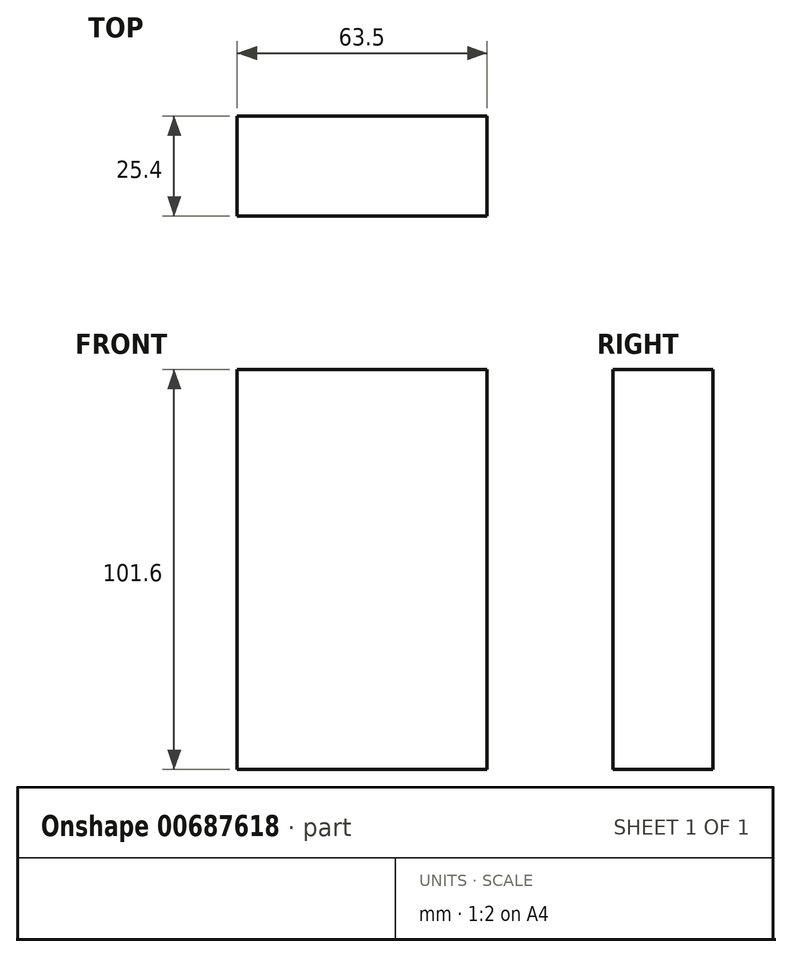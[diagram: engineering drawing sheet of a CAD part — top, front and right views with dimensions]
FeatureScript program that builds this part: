
annotation { "Feature Type Name" : "Feature", "Feature Type Description" : "" }
export const myFeature = defineFeature(function(context is Context, id is Id, definition is map)
    precondition{}
    {
        {
            var Q0;
            Q0=qCreatedBy(makeId("Front.planeOp"),FACE);
            var sketch = newSketch(context, id + "F0", { "sketchPlane" : qUnion([Q0])});
            skLineSegment(sketch, "E0.bottom", {"start": v(-39.98, 42.68) * mm, "end": v(23.52, 42.68) * mm});
            skLineSegment(sketch, "E0.top", {"start": v(-39.98, -58.92) * mm, "end": v(23.52, -58.92) * mm});
            skLineSegment(sketch, "E0.left", {"start": v(-39.98, 42.68) * mm, "end": v(-39.98, -58.92) * mm});
            skLineSegment(sketch, "E0.right", {"start": v(23.52, 42.68) * mm, "end": v(23.52, -58.92) * mm});
            skSolve(sketch);
        }
        {
            var Q0;
            Q0=makeQuery(id+"F0.imprint","IMPRINT",FACE,{"disambiguationData":[TD([[makeQuery(id+"F0.imprint","IMPRINT",EDGE,{"derivedFrom":sQuery(id+"F0.wireOp",EDGE,"E0.bottom")}),-1.0]])]});
            extrude(context, id + "F1", {"entities" : qUnion([Q0]), "depth" : 25.4 * mm, "offsetDistance" : 25.4 * mm});
        }
    });
